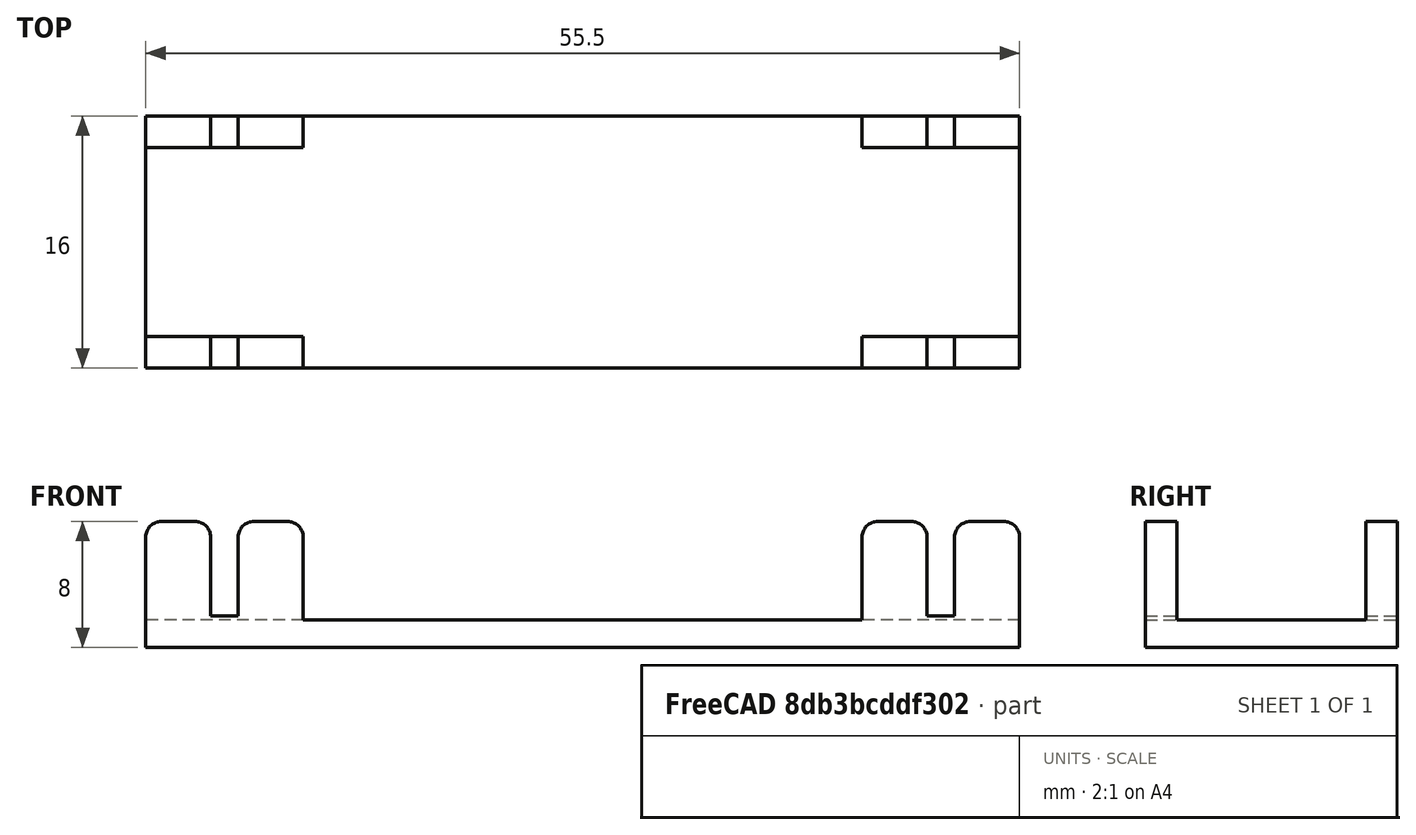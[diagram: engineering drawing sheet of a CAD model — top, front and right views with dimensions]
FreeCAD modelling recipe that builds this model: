
FCSTD DOCUMENT  (FreeCAD 0.19R24276 (Git))
Label: axleJig
License: All rights reserved
LicenseURL: http://en.wikipedia.org/wiki/All_rights_reserved
objects: Part::Box×9, Part::Cut×4, Part::Fillet×4, Spreadsheet::Sheet×1, Part::MultiFuse×1
note: 18 computed .brp shape members not serialized (recipe doc carries the construction recipe); baked Part::Feature solids carry a one-line shape summary decoded from their .brp

FEATURE [Part::Box] Box  label="Cube"
  AttacherType = Attacher::AttachEngine3D
  Height = 8
  Length = 10
  Width = 2
  expr: Width = <<data>>.post_thickness
FEATURE [Part::Box] Box001  label="Cube001"
  AttacherType = Attacher::AttachEngine3D
  Height = 10
  Length = 1.75
  Placement = pos=(4.125,0,2) rot=(0,0,1;0rad)
  Width = 2
  expr: .Placement.Base.x = <<data>>.post_wdith / 2 - <<data>>.axle_diameter / 2
  expr: Width = <<data>>.post_thickness
  expr: Length = <<data>>.axle_diameter
FEATURE [Part::Cut] Cut
  Base = -> Box
  Tool = -> Box001
FEATURE [Part::Fillet] Fillet  label="post01"
  Base = -> Cut
  Edges = 4 edges r=1: [Edge2,Edge13,Edge21,Edge22]
FEATURE [Part::Box] Box002  label="Cube002"
  AttacherType = Attacher::AttachEngine3D
  Height = 8
  Length = 10
  Width = 2
FEATURE [Part::Box] Box003  label="Cube003"
  AttacherType = Attacher::AttachEngine3D
  Height = 10
  Length = 1.75
  Placement = pos=(4.125,0,2) rot=(0,0,1;0rad)
  Width = 2
  expr: .Placement.Base.x = <<data>>.post_wdith / 2 - <<data>>.axle_diameter / 2
  expr: Width = <<data>>.post_thickness
  expr: Length = <<data>>.axle_diameter
FEATURE [Part::Cut] Cut001
  Base = -> Box002
  Tool = -> Box003
FEATURE [Part::Fillet] Fillet001  label="post002"
  Base = -> Cut001
  Edges = 4 edges r=1: [Edge2,Edge13,Edge21,Edge22]
  Placement = pos=(0,14,0) rot=(0,0,1;0rad)
  expr: .Placement.Base.y = <<data>>.axle_width + <<data>>.post_thickness
FEATURE [Part::Box] Box004  label="Cube004"
  AttacherType = Attacher::AttachEngine3D
  Height = 8
  Length = 10
  Width = 2
  expr: Width = <<data>>.post_thickness
FEATURE [Part::Box] Box005  label="Cube005"
  AttacherType = Attacher::AttachEngine3D
  Height = 10
  Length = 1.75
  Placement = pos=(4.125,0,2) rot=(0,0,1;0rad)
  Width = 2
  expr: .Placement.Base.x = <<data>>.post_wdith / 2 - <<data>>.axle_diameter / 2
  expr: Width = <<data>>.post_thickness
  expr: Length = <<data>>.axle_diameter
FEATURE [Part::Cut] Cut002
  Base = -> Box004
  Tool = -> Box005
FEATURE [Part::Fillet] Fillet002  label="post003"
  Base = -> Cut002
  Edges = 4 edges r=1: [Edge2,Edge13,Edge21,Edge22]
  Placement = pos=(45.5,0,0) rot=(0,0,1;0rad)
  expr: .Placement.Base.x = <<data>>.wheel_base
FEATURE [Part::Box] Box006  label="Cube006"
  AttacherType = Attacher::AttachEngine3D
  Height = 8
  Length = 10
  Width = 2
  expr: Width = <<data>>.post_thickness
FEATURE [Part::Box] Box007  label="Cube007"
  AttacherType = Attacher::AttachEngine3D
  Height = 10
  Length = 1.75
  Placement = pos=(4.125,0,2) rot=(0,0,1;0rad)
  Width = 2
  expr: .Placement.Base.x = <<data>>.post_wdith / 2 - <<data>>.axle_diameter / 2
  expr: Width = <<data>>.post_thickness
  expr: Length = <<data>>.axle_diameter
FEATURE [Part::Cut] Cut003
  Base = -> Box006
  Tool = -> Box007
FEATURE [Part::Fillet] Fillet003  label="post004"
  Base = -> Cut003
  Edges = 4 edges r=1: [Edge2,Edge13,Edge21,Edge22]
  Placement = pos=(45.5,14,0) rot=(0,0,1;0rad)
  expr: .Placement.Base.x = <<data>>.wheel_base
  expr: .Placement.Base.y = <<data>>.axle_width + <<data>>.post_thickness
FEATURE [Part::Box] Box008  label="Cube008"
  AttacherType = Attacher::AttachEngine3D
  Height = 1.75
  Length = 55.5
  Width = 16
  expr: Height = <<data>>.ride_height
  expr: Width = <<data>>.post_thickness * 2 + <<data>>.axle_width
  expr: Length = <<data>>.wheel_base + <<data>>.post_wdith
FEATURE [Spreadsheet::Sheet] Spreadsheet  label="data"
  cells = A4=wheel_base; B4(wheel_base)==45.5mm; A5=axle_width; B5(axle_width)==12mm; A6=ride_height; B6(ride_height)==1.75mm; A7=axle_diameter; B7(axle_diameter)==1.75mm; A8=post_wdith; B8(post_wdith)==10mm; A9=post_thickness; B9(post_thickness)==2mm; A10=wheel_diameter; B10(wheel_diameter)==11mm
FEATURE [Part::MultiFuse] Fusion  label="axlejig"
  Shapes = -> [Box008,Fillet,Fillet001,Fillet002,Fillet003]
